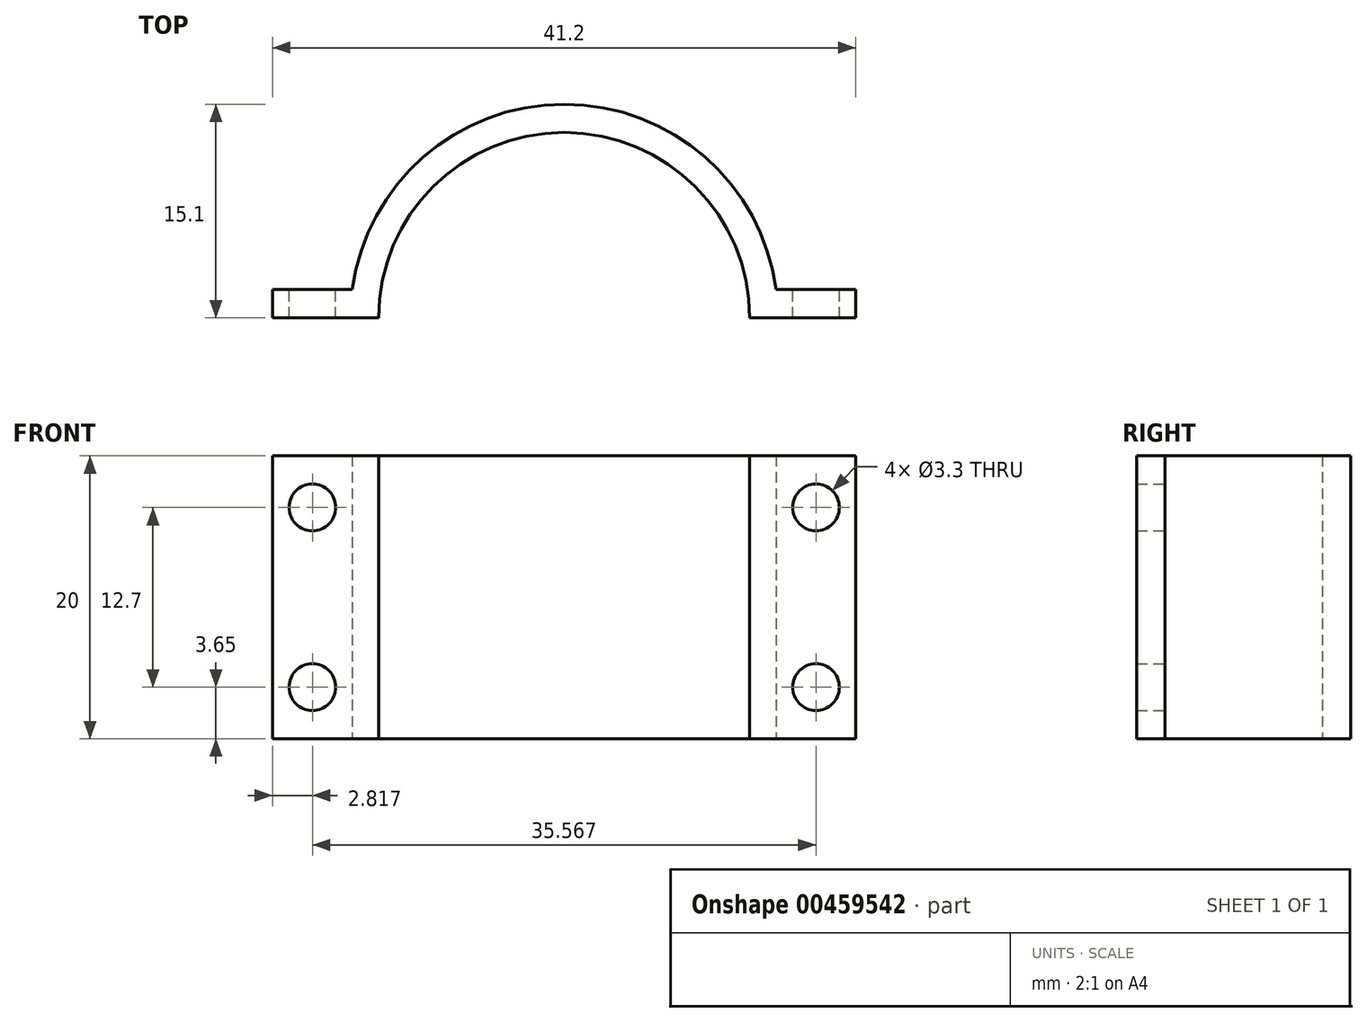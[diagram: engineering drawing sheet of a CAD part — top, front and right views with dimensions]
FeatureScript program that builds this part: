
annotation { "Feature Type Name" : "Feature", "Feature Type Description" : "" }
export const myFeature = defineFeature(function(context is Context, id is Id, definition is map)
    precondition{}
    {
        {
            var Q0;
            Q0=qCreatedBy(makeId("Top.planeOp"),FACE);
            var sketch = newSketch(context, id + "F0", { "sketchPlane" : qUnion([Q0])});
            skArc(sketch, "E0", {"start": v(13.1, 0) * mm, "mid": v(0, 13.1) * mm, "end": v(-13.1, 0) * mm});
            skLineSegment(sketch, "E1", {"start": v(-13.1, 0) * mm, "end": v(-20.6, 0) * mm});
            skLineSegment(sketch, "E2", {"start": v(-20.6, 0) * mm, "end": v(-20.6, 2) * mm});
            skLineSegment(sketch, "E3", {"start": v(-20.6, 2) * mm, "end": v(-14.97, 2) * mm});
            skLineSegment(sketch, "E4", {"start": v(13.1, 0) * mm, "end": v(20.6, 0) * mm});
            skLineSegment(sketch, "E5", {"start": v(20.6, 0) * mm, "end": v(20.6, 2) * mm});
            skLineSegment(sketch, "E6", {"start": v(20.6, 2) * mm, "end": v(14.97, 2) * mm});
            skArc(sketch, "E7.0", {"start": v(14.97, 2) * mm, "mid": v(0, 15.1) * mm, "end": v(-14.97, 2) * mm});
            skSolve(sketch);
        }
        {
            var Q0;
            Q0=makeQuery(id+"F0.imprint","IMPRINT",FACE,{"disambiguationData":[TD([[makeQuery(id+"F0.imprint","IMPRINT",EDGE,{"derivedFrom":sQuery(id+"F0.wireOp",EDGE,"E0")}),-1.0]])]});
            extrude(context, id + "F1", {"entities" : qUnion([Q0]), "depth" : 20 * mm, "offsetDistance" : 25 * mm});
        }
        {
            var Q0;
            Q0=makeQuery(id+"F1.opExtrude","SWEPT_FACE",FACE,{"disambiguationData":[OSD([sQuery(id+"F0.wireOp",EDGE,"E6")])]});
            var sketch = newSketch(context, id + "F2", { "sketchPlane" : qUnion([Q0])});
            skCircle(sketch, "E8", {"center": v(-17.78, 16.35) * mm, "radius": 1.65 * mm});
            skPoint(sketch, "E8.centerSnap0", {"position": v(-17.78, 20) * mm});
            skCircle(sketch, "E9", {"center": v(-17.78, 3.65) * mm, "radius": 1.65 * mm});
            skSolve(sketch);
        }
        {
            var Q0;
            Q0=makeQuery(id+"F1.opExtrude","SWEPT_FACE",FACE,{"disambiguationData":[OSD([sQuery(id+"F0.wireOp",EDGE,"E3")])]});
            var sketch = newSketch(context, id + "F3", { "sketchPlane" : qUnion([Q0])});
            skCircle(sketch, "E10", {"center": v(17.78, 16.35) * mm, "radius": 1.65 * mm});
            skPoint(sketch, "E10.centerSnap0", {"position": v(17.78, 20) * mm});
            skCircle(sketch, "E11", {"center": v(17.78, 3.65) * mm, "radius": 1.65 * mm});
            skSolve(sketch);
        }
        {
            var Q0;
            Q0=qSketchRegion(id+"F3",true);
            extrude(context, id + "F4", {"entities" : qUnion([Q0]), "operationType" : NewBodyOperationType.REMOVE, "oppositeDirection" : true, "depth" : 25 * mm, "offsetDistance" : 25 * mm});
        }
        {
            var Q0;
            Q0=makeQuery(id+"F2.imprint","IMPRINT",FACE,{"disambiguationData":[TD([[makeQuery(id+"F2.imprint","IMPRINT",EDGE,{"derivedFrom":sQuery(id+"F2.wireOp",EDGE,"E8")}),1.0]])]});
            var Q1;
            Q1=makeQuery(id+"F2.imprint","IMPRINT",FACE,{"disambiguationData":[TD([[makeQuery(id+"F2.imprint","IMPRINT",EDGE,{"derivedFrom":sQuery(id+"F2.wireOp",EDGE,"E9")}),1.0]])]});
            extrude(context, id + "F5", {"entities" : qUnion([Q0, Q1]), "operationType" : NewBodyOperationType.REMOVE, "oppositeDirection" : true, "depth" : 25 * mm, "offsetDistance" : 25 * mm});
        }
    });
